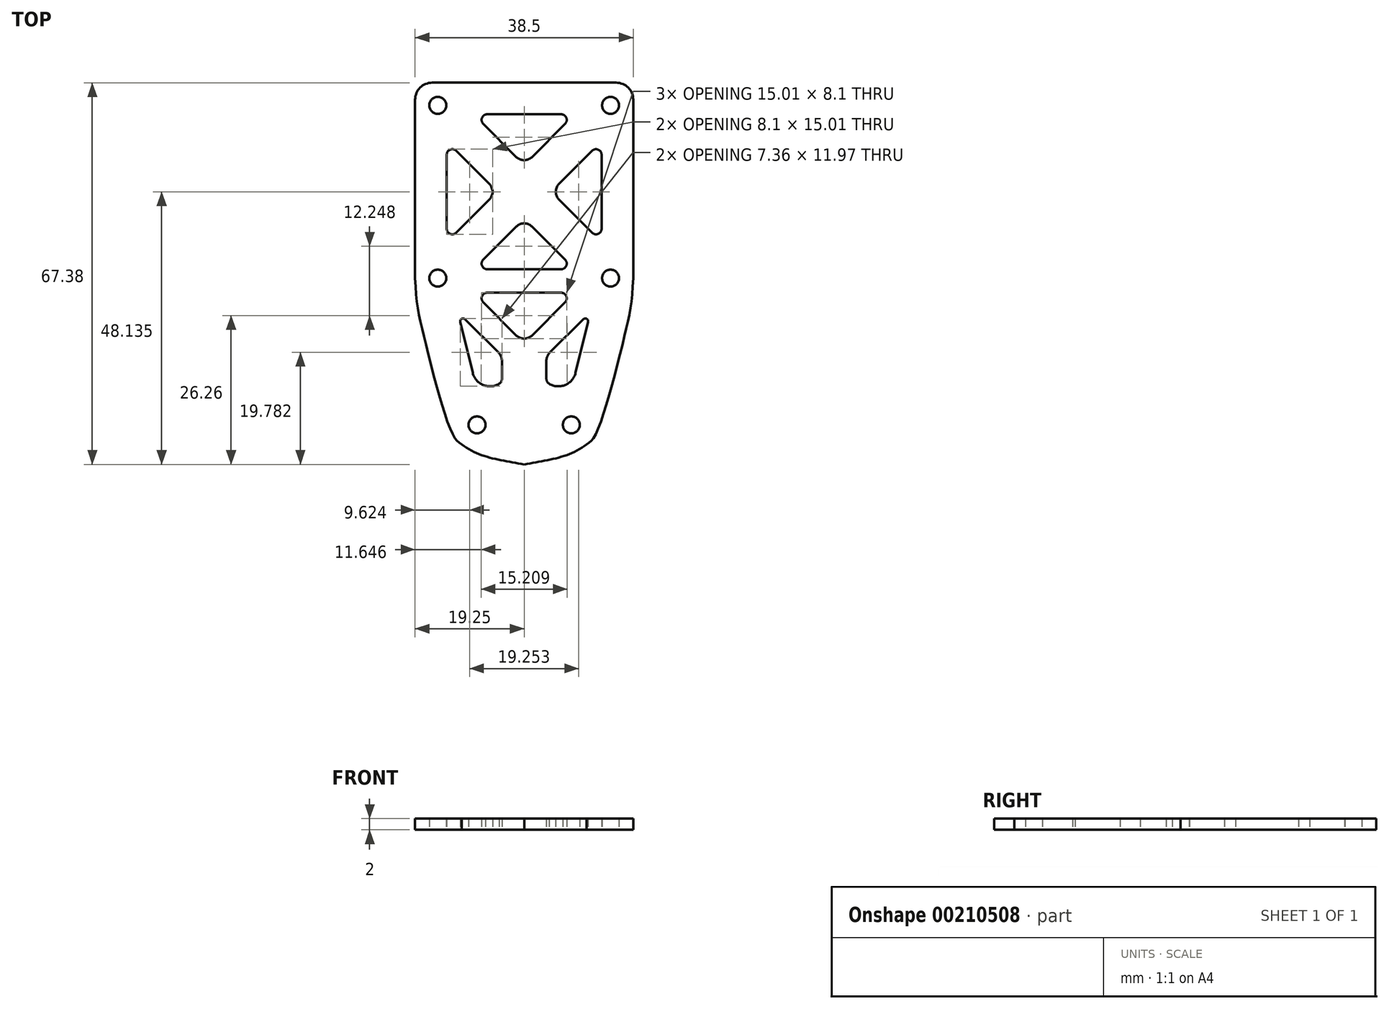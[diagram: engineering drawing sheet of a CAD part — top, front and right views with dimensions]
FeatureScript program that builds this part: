
annotation { "Feature Type Name" : "Feature", "Feature Type Description" : "" }
export const myFeature = defineFeature(function(context is Context, id is Id, definition is map)
    precondition{}
    {
        {
            var Q0;
            Q0=qCreatedBy(makeId("Top.planeOp"),FACE);
            var sketch = newSketch(context, id + "F0", { "sketchPlane" : qUnion([Q0])});
            skLineSegment(sketch, "E0.bottom", {"start": v(-15.28, 20.6) * mm, "end": v(15.22, 20.6) * mm, "construction": true});
            skLineSegment(sketch, "E0.top", {"start": v(-15.28, -9.9) * mm, "end": v(15.22, -9.9) * mm, "construction": true});
            skLineSegment(sketch, "E0.left", {"start": v(-15.28, 20.6) * mm, "end": v(-15.28, -9.9) * mm, "construction": true});
            skLineSegment(sketch, "E0.right", {"start": v(15.22, 20.6) * mm, "end": v(15.22, -9.9) * mm, "construction": true});
            skPoint(sketch, "E0.middle", {"position": v(-0.03, 5.34) * mm});
            skLineSegment(sketch, "E1.bottom", {"start": v(30.22, 35.6) * mm, "end": v(-30.28, 35.6) * mm, "construction": true});
            skLineSegment(sketch, "E1.top", {"start": v(30.22, -24.9) * mm, "end": v(-30.28, -24.9) * mm, "construction": true});
            skLineSegment(sketch, "E1.left", {"start": v(30.22, 35.6) * mm, "end": v(30.22, -24.9) * mm, "construction": true});
            skLineSegment(sketch, "E1.right", {"start": v(-30.28, 35.6) * mm, "end": v(-30.28, -24.9) * mm, "construction": true});
            skLineSegment(sketch, "E2.bottom", {"start": v(-70.99, 76.3) * mm, "end": v(70.93, 76.3) * mm, "construction": true});
            skLineSegment(sketch, "E2.top", {"start": v(-70.99, -65.62) * mm, "end": v(70.93, -65.62) * mm, "construction": true});
            skLineSegment(sketch, "E2.left", {"start": v(-70.99, 76.3) * mm, "end": v(-70.99, -65.62) * mm, "construction": true});
            skLineSegment(sketch, "E2.right", {"start": v(70.93, 76.3) * mm, "end": v(70.93, -65.62) * mm, "construction": true});
            skCircle(sketch, "E3", {"center": v(70.93, 76.3) * mm, "radius": 4.5 * mm, "construction": true});
            skCircle(sketch, "E4", {"center": v(-70.99, 76.3) * mm, "radius": 4.5 * mm, "construction": true});
            skCircle(sketch, "E5", {"center": v(70.93, -65.62) * mm, "radius": 4.5 * mm, "construction": true});
            skCircle(sketch, "E6", {"center": v(-70.99, -65.62) * mm, "radius": 4.5 * mm, "construction": true});
            skCircle(sketch, "E7", {"center": v(70.93, 76.3) * mm, "radius": 8 * mm, "construction": true});
            skCircle(sketch, "E8", {"center": v(70.93, -65.62) * mm, "radius": 8 * mm, "construction": true});
            skCircle(sketch, "E9", {"center": v(-70.99, -65.62) * mm, "radius": 8 * mm, "construction": true});
            skCircle(sketch, "E10", {"center": v(-70.99, 76.3) * mm, "radius": 8 * mm, "construction": true});
            skCircle(sketch, "E11", {"center": v(70.93, 76.3) * mm, "radius": 9.5 * mm, "construction": true});
            skCircle(sketch, "E12", {"center": v(70.93, -65.62) * mm, "radius": 9.5 * mm, "construction": true});
            skCircle(sketch, "E13", {"center": v(-70.99, -65.62) * mm, "radius": 9.5 * mm, "construction": true});
            skCircle(sketch, "E14", {"center": v(-70.99, 76.3) * mm, "radius": 9.5 * mm, "construction": true});
            skCircle(sketch, "E15", {"center": v(70.93, 76.3) * mm, "radius": 14 * mm, "construction": true});
            skCircle(sketch, "E16", {"center": v(-70.99, 76.3) * mm, "radius": 14 * mm, "construction": true});
            skCircle(sketch, "E17", {"center": v(70.93, -65.62) * mm, "radius": 14 * mm, "construction": true});
            skCircle(sketch, "E18", {"center": v(-70.99, -65.62) * mm, "radius": 14 * mm, "construction": true});
            skCircle(sketch, "E19", {"center": v(70.93, 76.3) * mm, "radius": 63.5 * mm, "construction": true});
            skCircle(sketch, "E20", {"center": v(70.93, -65.62) * mm, "radius": 63.5 * mm, "construction": true});
            skCircle(sketch, "E21", {"center": v(-70.99, -65.62) * mm, "radius": 63.5 * mm, "construction": true});
            skCircle(sketch, "E22", {"center": v(-70.99, 76.3) * mm, "radius": 63.5 * mm, "construction": true});
            skLineSegment(sketch, "E23", {"start": v(-0.03, 35.6) * mm, "end": v(-0.03, 39.09) * mm, "construction": true});
            skLineSegment(sketch, "E24", {"start": v(-0.03, 39.09) * mm, "end": v(-15.03, 39.09) * mm, "construction": true});
            skLineSegment(sketch, "E25", {"start": v(-0.03, 39.09) * mm, "end": v(14.97, 39.09) * mm, "construction": true});
            skLineSegment(sketch, "E26", {"start": v(-0.03, -24.9) * mm, "end": v(-0.03, -28.4) * mm, "construction": true});
            skLineSegment(sketch, "E27", {"start": v(-0.03, -28.4) * mm, "end": v(-15.03, -28.4) * mm, "construction": true});
            skLineSegment(sketch, "E28", {"start": v(-0.03, -28.4) * mm, "end": v(14.97, -28.4) * mm, "construction": true});
            skLineSegment(sketch, "E29.bottom", {"start": v(-26.22, 31.53) * mm, "end": v(26.16, 31.53) * mm, "construction": true});
            skLineSegment(sketch, "E29.top", {"start": v(-26.22, -20.85) * mm, "end": v(26.16, -20.85) * mm, "construction": true});
            skLineSegment(sketch, "E29.left", {"start": v(-26.22, 31.53) * mm, "end": v(-26.22, -20.85) * mm, "construction": true});
            skLineSegment(sketch, "E29.right", {"start": v(26.16, 31.53) * mm, "end": v(26.16, -20.85) * mm, "construction": true});
            skCircle(sketch, "E30", {"center": v(30.22, 35.6) * mm, "radius": 3.57 * mm, "construction": true});
            skCircle(sketch, "E31", {"center": v(-30.28, 35.6) * mm, "radius": 3.57 * mm, "construction": true});
            skCircle(sketch, "E32", {"center": v(30.22, -24.9) * mm, "radius": 3.57 * mm, "construction": true});
            skCircle(sketch, "E33", {"center": v(-30.28, -24.9) * mm, "radius": 3.57 * mm, "construction": true});
            skLineSegment(sketch, "E34", {"start": v(-70.99, 76.3) * mm, "end": v(70.93, -65.62) * mm, "construction": true});
            skLineSegment(sketch, "E35", {"start": v(-0.03, -20.85) * mm, "end": v(17.5, -20.85) * mm, "construction": true});
            skLineSegment(sketch, "E36", {"start": v(-0.03, -20.85) * mm, "end": v(-17.57, -20.85) * mm, "construction": true});
            skLineSegment(sketch, "E37", {"start": v(-0.03, -28.4) * mm, "end": v(-0.03, -39.26) * mm, "construction": true});
            skLineSegment(sketch, "E38", {"start": v(-0.03, -39.26) * mm, "end": v(-0.03, -42.8) * mm, "construction": true});
            skLineSegment(sketch, "E39", {"start": v(-0.03, -39.26) * mm, "end": v(10.97, -39.26) * mm, "construction": true});
            skLineSegment(sketch, "E40", {"start": v(-0.03, -39.26) * mm, "end": v(-11.03, -39.26) * mm, "construction": true});
            skLineSegment(sketch, "E41", {"start": v(-15.28, -9.9) * mm, "end": v(-19.28, -9.9) * mm, "construction": true});
            skLineSegment(sketch, "E42", {"start": v(15.22, -9.9) * mm, "end": v(19.22, -9.9) * mm, "construction": true});
            skLineSegment(sketch, "E43", {"start": v(15.22, 20.6) * mm, "end": v(19.22, 20.6) * mm, "construction": true});
            skLineSegment(sketch, "E44", {"start": v(-15.28, 20.6) * mm, "end": v(-19.28, 20.6) * mm, "construction": true});
            skLineSegment(sketch, "E45", {"start": v(-16.24, -26.62) * mm, "end": v(-0.03, -26.62) * mm, "construction": true});
            skLineSegment(sketch, "E46", {"start": v(-0.03, -26.62) * mm, "end": v(16.19, -26.62) * mm, "construction": true});
            skLineSegment(sketch, "E47", {"start": v(-12.63, -37.52) * mm, "end": v(-0.03, -37.52) * mm, "construction": true});
            skLineSegment(sketch, "E48", {"start": v(-0.03, -37.52) * mm, "end": v(12.57, -37.52) * mm, "construction": true});
            skFitSpline(sketch, "E49", {"points": [v(-11.03, -39.26) * mm, v(-0.03, -42.8) * mm], "startDerivative": vector(9.3, -7.23) * mm, "endDerivative": vector(12, -2.3) * mm});
            skFitSpline(sketch, "E50", {"points": [v(10.97, -39.26) * mm, v(-0.03, -42.8) * mm], "startDerivative": vector(-9.3, -7.23) * mm, "endDerivative": vector(-12, -2.3) * mm});
            skLineSegment(sketch, "E51", {"start": v(-7.93, -41.67) * mm, "end": v(-0.03, -41.67) * mm, "construction": true});
            skLineSegment(sketch, "E52", {"start": v(-0.03, -41.67) * mm, "end": v(7.87, -41.67) * mm, "construction": true});
            skLineSegment(sketch, "E53", {"start": v(-4.03, -42.03) * mm, "end": v(-0.03, -42.03) * mm, "construction": true});
            skLineSegment(sketch, "E54", {"start": v(-0.03, -42.03) * mm, "end": v(3.97, -42.03) * mm, "construction": true});
            skCircle(sketch, "E55", {"center": v(-8.36, -35.8) * mm, "radius": 1.5 * mm});
            skCircle(sketch, "E56", {"center": v(8.3, -35.8) * mm, "radius": 1.5 * mm});
            skLineSegment(sketch, "E57", {"start": v(-19.28, 20.6) * mm, "end": v(-19.28, -9.9) * mm});
            skLineSegment(sketch, "E58", {"start": v(19.22, 20.6) * mm, "end": v(19.22, -9.9) * mm});
            skLineSegment(sketch, "E59", {"start": v(15.52, 23.35) * mm, "end": v(-0.03, 23.35) * mm, "construction": true});
            skLineSegment(sketch, "E60", {"start": v(-0.03, 23.35) * mm, "end": v(-15.58, 23.35) * mm, "construction": true});
            skPoint(sketch, "E61.visualSharp", {"position": v(-17.57, -20.85) * mm});
            skPoint(sketch, "E62.visualSharp", {"position": v(17.5, -20.85) * mm});
            skFitSpline(sketch, "E63", {"points": [v(-19.28, -9.9) * mm, v(-17.57, -20.85) * mm, v(-12.63, -37.52) * mm, v(-11.03, -39.26) * mm], "startDerivative": vector(1.48, -36.7) * mm, "endDerivative": vector(10.67, -6.67) * mm});
            skFitSpline(sketch, "E64", {"points": [v(19.22, -9.9) * mm, v(17.5, -20.85) * mm, v(12.57, -37.52) * mm, v(10.97, -39.26) * mm], "startDerivative": vector(-1.5, -36.7) * mm, "endDerivative": vector(-10.67, -6.67) * mm});
            skLineSegment(sketch, "E65", {"start": v(-8.36, -35.8) * mm, "end": v(-13.36, -35.8) * mm, "construction": true});
            skLineSegment(sketch, "E66", {"start": v(-8.36, -35.8) * mm, "end": v(-8.36, -40.8) * mm, "construction": true});
            skLineSegment(sketch, "E67", {"start": v(8.3, -35.8) * mm, "end": v(13.3, -35.8) * mm, "construction": true});
            skLineSegment(sketch, "E68", {"start": v(8.3, -35.8) * mm, "end": v(8.3, -40.8) * mm, "construction": true});
            skCircle(sketch, "E69", {"center": v(-15.28, 20.6) * mm, "radius": 1.5 * mm});
            skCircle(sketch, "E70", {"center": v(15.22, 20.6) * mm, "radius": 1.5 * mm});
            skCircle(sketch, "E71", {"center": v(15.22, -9.9) * mm, "radius": 1.5 * mm});
            skCircle(sketch, "E72", {"center": v(-15.28, -9.9) * mm, "radius": 1.5 * mm});
            skLineSegment(sketch, "E73.bottom", {"start": v(-13.7, 19.02) * mm, "end": v(13.65, 19.02) * mm, "construction": true});
            skLineSegment(sketch, "E73.top", {"start": v(-13.7, -8.33) * mm, "end": v(13.65, -8.33) * mm, "construction": true});
            skLineSegment(sketch, "E73.left", {"start": v(-13.7, 19.02) * mm, "end": v(-13.7, -8.33) * mm, "construction": true});
            skLineSegment(sketch, "E73.right", {"start": v(13.65, 19.02) * mm, "end": v(13.65, -8.33) * mm, "construction": true});
            skLineSegment(sketch, "E74.bottom", {"start": v(-4.78, 10.1) * mm, "end": v(4.72, 10.1) * mm, "construction": true});
            skLineSegment(sketch, "E74.top", {"start": v(-4.78, 0.6) * mm, "end": v(4.72, 0.6) * mm, "construction": true});
            skLineSegment(sketch, "E74.left", {"start": v(-4.78, 10.1) * mm, "end": v(-4.78, 0.6) * mm, "construction": true});
            skLineSegment(sketch, "E74.right", {"start": v(4.72, 10.1) * mm, "end": v(4.72, 0.6) * mm, "construction": true});
            skPoint(sketch, "E75", {"position": v(-4.78, 5.34) * mm});
            skPoint(sketch, "E76", {"position": v(-0.03, 10.1) * mm});
            skPoint(sketch, "E77", {"position": v(4.72, 5.34) * mm});
            skPoint(sketch, "E78", {"position": v(-0.03, 0.6) * mm});
            skLineSegment(sketch, "E79", {"start": v(-6.2, 6.76) * mm, "end": v(-12, 12.56) * mm});
            skLineSegment(sketch, "E80", {"start": v(-6.2, 3.93) * mm, "end": v(-12, -1.87) * mm});
            skLineSegment(sketch, "E81", {"start": v(-13.7, -1.17) * mm, "end": v(-13.7, 11.86) * mm});
            skLineSegment(sketch, "E82", {"start": v(6.13, 3.93) * mm, "end": v(11.94, -1.87) * mm});
            skLineSegment(sketch, "E83", {"start": v(6.13, 6.76) * mm, "end": v(11.94, 12.56) * mm});
            skLineSegment(sketch, "E84", {"start": v(13.65, 11.86) * mm, "end": v(13.65, -1.17) * mm});
            skArc(sketch, "E85.filletArc", {"start": v(-6.2, 3.93) * mm, "mid": v(-5.6, 5.34) * mm, "end": v(-6.2, 6.76) * mm});
            skPoint(sketch, "E86.visualSharp", {"position": v(-13.7, 14.27) * mm});
            skArc(sketch, "E86.filletArc", {"start": v(-12, 12.56) * mm, "mid": v(-13.09, 12.78) * mm, "end": v(-13.7, 11.86) * mm});
            skPoint(sketch, "E87.visualSharp", {"position": v(-13.7, -3.58) * mm});
            skArc(sketch, "E87.filletArc", {"start": v(-13.7, -1.17) * mm, "mid": v(-13.09, -2.09) * mm, "end": v(-12, -1.87) * mm});
            skArc(sketch, "E88.filletArc", {"start": v(6.13, 6.76) * mm, "mid": v(5.55, 5.34) * mm, "end": v(6.13, 3.93) * mm});
            skPoint(sketch, "E89.visualSharp", {"position": v(13.65, 14.27) * mm});
            skArc(sketch, "E89.filletArc", {"start": v(13.65, 11.86) * mm, "mid": v(13.03, 12.78) * mm, "end": v(11.94, 12.56) * mm});
            skPoint(sketch, "E90.visualSharp", {"position": v(13.65, -3.58) * mm});
            skArc(sketch, "E90.filletArc", {"start": v(11.94, -1.87) * mm, "mid": v(13.03, -2.09) * mm, "end": v(13.65, -1.17) * mm});
            skLineSegment(sketch, "E91", {"start": v(1.38, -0.82) * mm, "end": v(7.19, -6.62) * mm});
            skLineSegment(sketch, "E92", {"start": v(-1.44, -0.82) * mm, "end": v(-7.25, -6.62) * mm});
            skLineSegment(sketch, "E93", {"start": v(-6.54, -8.33) * mm, "end": v(6.48, -8.33) * mm});
            skArc(sketch, "E94.filletArc", {"start": v(1.38, -0.82) * mm, "mid": v(-0.03, -0.23) * mm, "end": v(-1.44, -0.82) * mm});
            skPoint(sketch, "E95.visualSharp", {"position": v(8.9, -8.33) * mm});
            skArc(sketch, "E95.filletArc", {"start": v(6.48, -8.33) * mm, "mid": v(7.4, -7.71) * mm, "end": v(7.19, -6.62) * mm});
            skPoint(sketch, "E96.visualSharp", {"position": v(-8.95, -8.33) * mm});
            skArc(sketch, "E96.filletArc", {"start": v(-7.25, -6.62) * mm, "mid": v(-7.46, -7.71) * mm, "end": v(-6.54, -8.33) * mm});
            skLineSegment(sketch, "E97", {"start": v(-0.03, -12.48) * mm, "end": v(13.33, -12.48) * mm, "construction": true});
            skPoint(sketch, "E98", {"position": v(-0.03, -12.48) * mm});
            skLineSegment(sketch, "E99", {"start": v(-0.03, -12.48) * mm, "end": v(-13.39, -12.48) * mm, "construction": true});
            skLineSegment(sketch, "E100", {"start": v(-8.95, -8.33) * mm, "end": v(-8.95, -12.48) * mm, "construction": true});
            skLineSegment(sketch, "E101", {"start": v(8.9, -8.33) * mm, "end": v(8.9, -12.48) * mm, "construction": true});
            skLineSegment(sketch, "E102", {"start": v(-0.03, -12.48) * mm, "end": v(-0.03, -21.4) * mm, "construction": true});
            skLineSegment(sketch, "E103", {"start": v(-7.25, -14.19) * mm, "end": v(-1.44, -20) * mm});
            skLineSegment(sketch, "E104", {"start": v(1.38, -20) * mm, "end": v(7.19, -14.19) * mm});
            skLineSegment(sketch, "E105", {"start": v(6.48, -12.48) * mm, "end": v(-6.54, -12.48) * mm});
            skPoint(sketch, "E106.visualSharp", {"position": v(-8.95, -12.48) * mm});
            skArc(sketch, "E106.filletArc", {"start": v(-6.54, -12.48) * mm, "mid": v(-7.46, -13.1) * mm, "end": v(-7.25, -14.19) * mm});
            skPoint(sketch, "E107.visualSharp", {"position": v(8.9, -12.48) * mm});
            skArc(sketch, "E107.filletArc", {"start": v(7.19, -14.19) * mm, "mid": v(7.4, -13.1) * mm, "end": v(6.48, -12.48) * mm});
            skPoint(sketch, "E108.visualSharp", {"position": v(-0.03, -21.4) * mm});
            skArc(sketch, "E108.filletArc", {"start": v(-1.44, -20) * mm, "mid": v(-0.03, -20.58) * mm, "end": v(1.38, -20) * mm});
            skLineSegment(sketch, "E109", {"start": v(-0.03, -15.9) * mm, "end": v(-11.73, -15.9) * mm, "construction": true});
            skLineSegment(sketch, "E110", {"start": v(-0.03, -15.9) * mm, "end": v(11.67, -15.9) * mm, "construction": true});
            skLineSegment(sketch, "E111", {"start": v(-10.46, -17.16) * mm, "end": v(-4.54, -23.1) * mm});
            skLineSegment(sketch, "E112", {"start": v(-3.95, -24.5) * mm, "end": v(-3.95, -27.68) * mm});
            skLineSegment(sketch, "E113", {"start": v(-11.3, -17.64) * mm, "end": v(-9.1, -26.62) * mm});
            skArc(sketch, "E114", {"start": v(-9.1, -26.62) * mm, "mid": v(-6.97, -28.87) * mm, "end": v(-3.95, -28.18) * mm, "construction": true});
            skLineSegment(sketch, "E115", {"start": v(-4.35, -28.48) * mm, "end": v(-4.43, -28.54) * mm});
            skPoint(sketch, "E116", {"position": v(-6.97, -28.87) * mm});
            skArc(sketch, "E117", {"start": v(-9.1, -26.62) * mm, "mid": v(-7.25, -28.77) * mm, "end": v(-4.43, -28.54) * mm});
            skPoint(sketch, "E118.visualSharp", {"position": v(-11.73, -15.9) * mm});
            skArc(sketch, "E118.filletArc", {"start": v(-10.46, -17.16) * mm, "mid": v(-11.06, -17.08) * mm, "end": v(-11.3, -17.64) * mm});
            skPoint(sketch, "E119.visualSharp", {"position": v(-3.95, -23.68) * mm});
            skArc(sketch, "E119.filletArc", {"start": v(-3.95, -24.5) * mm, "mid": v(-4.1, -23.74) * mm, "end": v(-4.54, -23.1) * mm});
            skPoint(sketch, "E120.visualSharp", {"position": v(-3.95, -28.18) * mm});
            skArc(sketch, "E120.filletArc", {"start": v(-4.35, -28.48) * mm, "mid": v(-4.06, -28.13) * mm, "end": v(-3.95, -27.68) * mm});
            skLineSegment(sketch, "E121", {"start": v(10.4, -17.16) * mm, "end": v(4.48, -23.1) * mm});
            skLineSegment(sketch, "E122", {"start": v(3.9, -24.5) * mm, "end": v(3.9, -27.68) * mm});
            skLineSegment(sketch, "E123", {"start": v(3.9, -26.62) * mm, "end": v(9.04, -26.62) * mm, "construction": true});
            skArc(sketch, "E124", {"start": v(3.9, -28.18) * mm, "mid": v(6.91, -28.87) * mm, "end": v(9.04, -26.62) * mm, "construction": true});
            skLineSegment(sketch, "E125", {"start": v(11.24, -17.64) * mm, "end": v(9.04, -26.62) * mm});
            skLineSegment(sketch, "E126", {"start": v(4.29, -28.48) * mm, "end": v(4.37, -28.54) * mm});
            skPoint(sketch, "E127", {"position": v(6.91, -28.87) * mm});
            skArc(sketch, "E128", {"start": v(4.37, -28.54) * mm, "mid": v(7.2, -28.77) * mm, "end": v(9.04, -26.62) * mm});
            skPoint(sketch, "E129.visualSharp", {"position": v(3.9, -23.68) * mm});
            skArc(sketch, "E129.filletArc", {"start": v(4.48, -23.1) * mm, "mid": v(4.04, -23.74) * mm, "end": v(3.9, -24.5) * mm});
            skPoint(sketch, "E130.visualSharp", {"position": v(3.9, -28.18) * mm});
            skArc(sketch, "E130.filletArc", {"start": v(3.9, -27.68) * mm, "mid": v(4, -28.13) * mm, "end": v(4.29, -28.48) * mm});
            skPoint(sketch, "E131.visualSharp", {"position": v(11.67, -15.9) * mm});
            skArc(sketch, "E131.filletArc", {"start": v(11.24, -17.64) * mm, "mid": v(11, -17.08) * mm, "end": v(10.4, -17.16) * mm});
            skLineSegment(sketch, "E132", {"start": v(-8.95, -8.33) * mm, "end": v(-8.95, 19.02) * mm, "construction": true});
            skLineSegment(sketch, "E133", {"start": v(8.9, -8.33) * mm, "end": v(8.9, 19.02) * mm, "construction": true});
            skLineSegment(sketch, "E134", {"start": v(-1.44, 11.5) * mm, "end": v(-7.25, 17.31) * mm});
            skLineSegment(sketch, "E135", {"start": v(1.38, 11.5) * mm, "end": v(7.19, 17.31) * mm});
            skLineSegment(sketch, "E136", {"start": v(6.48, 19.02) * mm, "end": v(-6.54, 19.02) * mm});
            skArc(sketch, "E137.filletArc", {"start": v(-1.44, 11.5) * mm, "mid": v(-0.03, 10.92) * mm, "end": v(1.38, 11.5) * mm});
            skPoint(sketch, "E138.visualSharp", {"position": v(8.9, 19.02) * mm});
            skArc(sketch, "E138.filletArc", {"start": v(7.19, 17.31) * mm, "mid": v(7.4, 18.4) * mm, "end": v(6.48, 19.02) * mm});
            skPoint(sketch, "E139.visualSharp", {"position": v(-8.95, 19.02) * mm});
            skArc(sketch, "E139.filletArc", {"start": v(-6.54, 19.02) * mm, "mid": v(-7.46, 18.4) * mm, "end": v(-7.25, 17.31) * mm});
            skLineSegment(sketch, "E140", {"start": v(-0.03, 37.34) * mm, "end": v(8.47, 37.34) * mm, "construction": true});
            skPoint(sketch, "E140.endSnap0", {"position": v(-0.03, 37.34) * mm});
            skLineSegment(sketch, "E141", {"start": v(-0.03, 37.34) * mm, "end": v(-8.53, 37.34) * mm, "construction": true});
            skLineSegment(sketch, "E142", {"start": v(-15.28, 20.6) * mm, "end": v(-15.28, 24.6) * mm, "construction": true});
            skLineSegment(sketch, "E143", {"start": v(15.22, 20.6) * mm, "end": v(15.22, 24.6) * mm, "construction": true});
            skLineSegment(sketch, "E144", {"start": v(0, 24.6) * mm, "end": v(-16.28, 24.6) * mm});
            skLineSegment(sketch, "E145", {"start": v(0, 24.6) * mm, "end": v(16.22, 24.6) * mm});
            skLineSegment(sketch, "E146", {"start": v(19.22, 21.6) * mm, "end": v(19.22, 20.6) * mm});
            skLineSegment(sketch, "E147", {"start": v(-19.28, 21.6) * mm, "end": v(-19.28, 20.6) * mm});
            skPoint(sketch, "E148.visualSharp", {"position": v(-19.28, 24.6) * mm});
            skArc(sketch, "E148.filletArc", {"start": v(-16.28, 24.6) * mm, "mid": v(-18.4, 23.72) * mm, "end": v(-19.28, 21.6) * mm});
            skPoint(sketch, "E149.visualSharp", {"position": v(19.22, 24.6) * mm});
            skArc(sketch, "E149.filletArc", {"start": v(19.22, 21.6) * mm, "mid": v(18.34, 23.72) * mm, "end": v(16.22, 24.6) * mm});
            skSolve(sketch);
        }
        {
            var Q0;
            Q0 = qSketchRegion(id + "F0", true);
            extrude(context, id + "F1", {"entities" : qUnion([Q0]), "depth" : 2 * mm});
        }
    });
